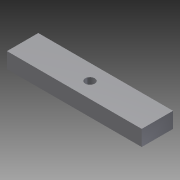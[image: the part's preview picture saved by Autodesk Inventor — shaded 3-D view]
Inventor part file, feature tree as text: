
AUTODESK INVENTOR PART (.ipt)
format: ipt  version: 2012 (Build 160160000, 160)  size: 73,728 bytes
history: native  units: mm
features: extrude x1, sketch x1
ambient origin geometry x8: Origin, YZ Plane, XZ Plane, XY Plane, X Axis, Y Axis, Z Axis, Center Point
bodies: Solid1 (feature_tree)
feature tree (2):
  extrude  "Extrusion1"  Depth=3.0mm
  sketch  "Sketch1"  dims[d0=3.0mm d1=5.0mm d2=21.5mm d3=3.0mm d4=5.0mm d5=21.5mm d6=5.0mm d7=0.0mm]
